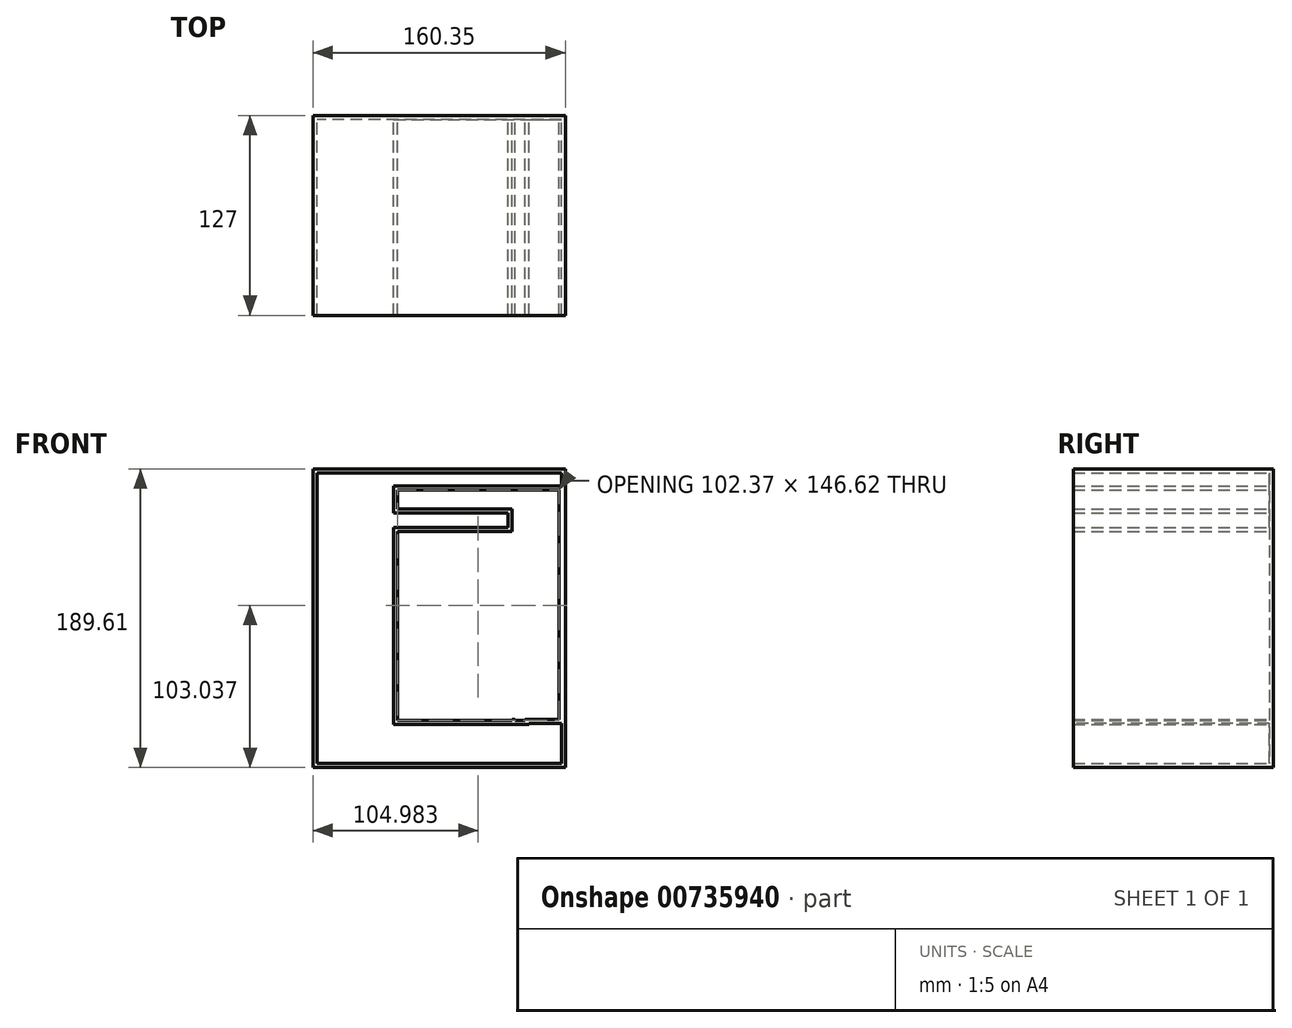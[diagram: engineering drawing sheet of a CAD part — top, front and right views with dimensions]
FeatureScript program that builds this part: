
annotation { "Feature Type Name" : "Feature", "Feature Type Description" : "" }
export const myFeature = defineFeature(function(context is Context, id is Id, definition is map)
    precondition{}
    {
        {
            var Q0;
            Q0=qCreatedBy(makeId("Front.planeOp"),FACE);
            var sketch = newSketch(context, id + "F0", { "sketchPlane" : qUnion([Q0])});
            skLineSegment(sketch, "E0.bottom", {"start": v(-170.01, -40.46) * mm, "end": v(-114.12, -40.46) * mm});
            skLineSegment(sketch, "E0.top", {"start": v(-170.01, -57.23) * mm, "end": v(-114.12, -57.23) * mm});
            skLineSegment(sketch, "E0.left", {"start": v(-170.01, -40.46) * mm, "end": v(-170.01, -57.23) * mm});
            skLineSegment(sketch, "E0.right", {"start": v(-114.12, -40.46) * mm, "end": v(-114.12, -57.23) * mm});
            skLineSegment(sketch, "E1.bottom", {"start": v(-170.01, -40.46) * mm, "end": v(-116.21, -40.46) * mm});
            skLineSegment(sketch, "E1.top", {"start": v(-170.01, 40.36) * mm, "end": v(-116.21, 40.36) * mm});
            skLineSegment(sketch, "E1.left", {"start": v(-170.01, -40.46) * mm, "end": v(-170.01, 40.36) * mm});
            skLineSegment(sketch, "E1.right", {"start": v(-116.21, -40.46) * mm, "end": v(-116.21, 40.36) * mm});
            skLineSegment(sketch, "E2.bottom", {"start": v(-116.21, 40.36) * mm, "end": v(-74.95, 40.36) * mm});
            skLineSegment(sketch, "E2.top", {"start": v(-116.21, -40.46) * mm, "end": v(-74.95, -40.46) * mm});
            skLineSegment(sketch, "E2.left", {"start": v(-116.21, 40.36) * mm, "end": v(-116.21, -40.46) * mm});
            skLineSegment(sketch, "E2.right", {"start": v(-74.95, 40.36) * mm, "end": v(-74.95, -40.46) * mm});
            skLineSegment(sketch, "E3.bottom", {"start": v(-74.95, -40.46) * mm, "end": v(-116.21, -40.46) * mm});
            skLineSegment(sketch, "E3.top", {"start": v(-74.95, -79.7) * mm, "end": v(-116.21, -79.7) * mm});
            skLineSegment(sketch, "E3.left", {"start": v(-74.95, -40.46) * mm, "end": v(-74.95, -79.7) * mm});
            skLineSegment(sketch, "E3.right", {"start": v(-116.21, -40.46) * mm, "end": v(-116.21, -79.7) * mm});
            skLineSegment(sketch, "E4.bottom", {"start": v(-74.95, -79.7) * mm, "end": v(-43.61, -79.7) * mm});
            skLineSegment(sketch, "E4.top", {"start": v(-74.95, -32.7) * mm, "end": v(-43.61, -32.7) * mm});
            skLineSegment(sketch, "E4.left", {"start": v(-74.95, -79.7) * mm, "end": v(-74.95, -32.7) * mm});
            skLineSegment(sketch, "E4.right", {"start": v(-43.61, -79.7) * mm, "end": v(-43.61, -32.7) * mm});
            skLineSegment(sketch, "E5.bottom", {"start": v(-43.61, -32.7) * mm, "end": v(-74.95, -32.7) * mm});
            skLineSegment(sketch, "E5.top", {"start": v(-43.61, 6.98) * mm, "end": v(-74.95, 6.98) * mm});
            skLineSegment(sketch, "E5.left", {"start": v(-43.61, -32.7) * mm, "end": v(-43.61, 6.98) * mm});
            skLineSegment(sketch, "E5.right", {"start": v(-74.95, -32.7) * mm, "end": v(-74.95, 6.98) * mm});
            skLineSegment(sketch, "E6.bottom", {"start": v(-74.95, 40.36) * mm, "end": v(-43.61, 40.36) * mm});
            skLineSegment(sketch, "E6.top", {"start": v(-74.95, 6.98) * mm, "end": v(-43.61, 6.98) * mm});
            skLineSegment(sketch, "E6.left", {"start": v(-74.95, 40.36) * mm, "end": v(-74.95, 6.98) * mm});
            skLineSegment(sketch, "E6.right", {"start": v(-43.61, 40.36) * mm, "end": v(-43.61, 6.98) * mm});
            skLineSegment(sketch, "E7.bottom", {"start": v(-43.61, 40.36) * mm, "end": v(-13.84, 40.36) * mm});
            skLineSegment(sketch, "E7.top", {"start": v(-43.61, 54.76) * mm, "end": v(-13.84, 54.76) * mm});
            skLineSegment(sketch, "E7.left", {"start": v(-43.61, 40.36) * mm, "end": v(-43.61, 54.76) * mm});
            skLineSegment(sketch, "E7.right", {"start": v(-13.84, 40.36) * mm, "end": v(-13.84, 54.76) * mm});
            skLineSegment(sketch, "E8.bottom", {"start": v(-13.84, 54.76) * mm, "end": v(-43.61, 54.76) * mm});
            skLineSegment(sketch, "E8.top", {"start": v(-13.84, 6.98) * mm, "end": v(-43.61, 6.98) * mm});
            skLineSegment(sketch, "E8.left", {"start": v(-13.84, 54.76) * mm, "end": v(-13.84, 6.98) * mm});
            skLineSegment(sketch, "E8.right", {"start": v(-43.61, 54.76) * mm, "end": v(-43.61, 6.98) * mm});
            skLineSegment(sketch, "E9.top", {"start": v(-13.84, -32.7) * mm, "end": v(-43.61, -32.7) * mm});
            skLineSegment(sketch, "E9.left", {"start": v(-13.84, 6.98) * mm, "end": v(-13.84, -32.7) * mm});
            skLineSegment(sketch, "E9.right", {"start": v(-43.61, 6.98) * mm, "end": v(-43.61, -32.7) * mm});
            skLineSegment(sketch, "E10.bottom", {"start": v(-41.52, -32.62) * mm, "end": v(-35.26, -32.62) * mm});
            skLineSegment(sketch, "E10.top", {"start": v(-41.52, -79.7) * mm, "end": v(-35.26, -79.7) * mm});
            skLineSegment(sketch, "E10.left", {"start": v(-41.52, -32.62) * mm, "end": v(-41.52, -79.7) * mm});
            skLineSegment(sketch, "E10.right", {"start": v(-35.26, -32.62) * mm, "end": v(-35.26, -79.7) * mm});
            skLineSegment(sketch, "E11.bottom", {"start": v(-35.26, -78.86) * mm, "end": v(-13.84, -78.86) * mm});
            skLineSegment(sketch, "E11.top", {"start": v(-35.26, -32.7) * mm, "end": v(-13.84, -32.7) * mm});
            skLineSegment(sketch, "E11.left", {"start": v(-35.26, -78.86) * mm, "end": v(-35.26, -32.7) * mm});
            skLineSegment(sketch, "E11.right", {"start": v(-13.84, -78.86) * mm, "end": v(-13.84, -32.7) * mm});
            skLineSegment(sketch, "E12.bottom", {"start": v(-170.01, -57.23) * mm, "end": v(-116.21, -57.23) * mm});
            skLineSegment(sketch, "E12.top", {"start": v(-170.01, -79.7) * mm, "end": v(-116.21, -79.7) * mm});
            skLineSegment(sketch, "E12.left", {"start": v(-170.01, -57.23) * mm, "end": v(-170.01, -79.7) * mm});
            skLineSegment(sketch, "E12.right", {"start": v(-116.21, -57.23) * mm, "end": v(-116.21, -79.7) * mm});
            skLineSegment(sketch, "E13.bottom", {"start": v(-170.01, 40.36) * mm, "end": v(-43.61, 40.36) * mm});
            skLineSegment(sketch, "E13.top", {"start": v(-170.01, 54.76) * mm, "end": v(-43.61, 54.76) * mm});
            skLineSegment(sketch, "E13.left", {"start": v(-170.01, 40.36) * mm, "end": v(-170.01, 54.76) * mm});
            skLineSegment(sketch, "E14.bottom", {"start": v(-170.01, 54.76) * mm, "end": v(-116.21, 54.76) * mm});
            skLineSegment(sketch, "E14.top", {"start": v(-170.01, 66.93) * mm, "end": v(-116.21, 66.93) * mm});
            skLineSegment(sketch, "E14.left", {"start": v(-170.01, 54.76) * mm, "end": v(-170.01, 66.93) * mm});
            skLineSegment(sketch, "E14.right", {"start": v(-116.21, 54.76) * mm, "end": v(-116.21, 66.93) * mm});
            skLineSegment(sketch, "E15.bottom", {"start": v(-116.21, 66.93) * mm, "end": v(-43.61, 66.93) * mm});
            skLineSegment(sketch, "E15.top", {"start": v(-116.21, 54.76) * mm, "end": v(-43.61, 54.76) * mm});
            skLineSegment(sketch, "E15.left", {"start": v(-116.21, 66.93) * mm, "end": v(-116.21, 54.76) * mm});
            skLineSegment(sketch, "E15.right", {"start": v(-43.61, 66.93) * mm, "end": v(-43.61, 54.76) * mm});
            skLineSegment(sketch, "E16.bottom", {"start": v(-43.61, 66.93) * mm, "end": v(-13.84, 66.93) * mm});
            skLineSegment(sketch, "E16.right", {"start": v(-13.84, 66.93) * mm, "end": v(-13.84, 54.76) * mm});
            skLineSegment(sketch, "E17.bottom", {"start": v(-9.66, 66.93) * mm, "end": v(-170.01, 66.93) * mm});
            skLineSegment(sketch, "E17.top", {"start": v(-9.66, 80.2) * mm, "end": v(-170.01, 80.2) * mm});
            skLineSegment(sketch, "E17.left", {"start": v(-9.66, 66.93) * mm, "end": v(-9.66, 80.2) * mm});
            skLineSegment(sketch, "E17.right", {"start": v(-170.01, 66.93) * mm, "end": v(-170.01, 80.2) * mm});
            skLineSegment(sketch, "E18.bottom", {"start": v(-9.66, 66.93) * mm, "end": v(-13.84, 66.93) * mm});
            skLineSegment(sketch, "E18.top", {"start": v(-9.66, -78.86) * mm, "end": v(-13.84, -78.86) * mm});
            skLineSegment(sketch, "E18.left", {"start": v(-9.66, 66.93) * mm, "end": v(-9.66, -78.86) * mm});
            skLineSegment(sketch, "E18.right", {"start": v(-13.84, 66.93) * mm, "end": v(-13.84, -78.86) * mm});
            skLineSegment(sketch, "E19.bottom", {"start": v(-9.66, -78.86) * mm, "end": v(-170.01, -78.86) * mm});
            skLineSegment(sketch, "E19.top", {"start": v(-9.66, -109.42) * mm, "end": v(-170.01, -109.42) * mm});
            skLineSegment(sketch, "E19.left", {"start": v(-9.66, -78.86) * mm, "end": v(-9.66, -109.42) * mm});
            skLineSegment(sketch, "E19.right", {"start": v(-170.01, -78.86) * mm, "end": v(-170.01, -109.42) * mm});
            skSolve(sketch);
        }
        {
            var Q0;
            Q0 = qSketchRegion(id + "F0", true);
            extrude(context, id + "F1", {"entities" : qUnion([Q0]), "depth" : 127 * mm, "offsetDistance" : 25.4 * mm});
        }
        {
            var Q0;
            Q0=makeQuery(id+"F1.opExtrude","CAP_FACE",FACE,{"disambiguationData":[OSD([sQuery(id+"F0.wireOp",EDGE,"E0.left"),sQuery(id+"F0.wireOp",EDGE,"E1.left"),sQuery(id+"F0.wireOp",EDGE,"E2.left"),sQuery(id+"F0.wireOp",EDGE,"E3.top"),sQuery(id+"F0.wireOp",EDGE,"E3.right"),sQuery(id+"F0.wireOp",EDGE,"E4.bottom"),sQuery(id+"F0.wireOp",EDGE,"E4.right"),sQuery(id+"F0.wireOp",EDGE,"E10.top"),sQuery(id+"F0.wireOp",EDGE,"E10.left"),sQuery(id+"F0.wireOp",EDGE,"E10.right"),sQuery(id+"F0.wireOp",EDGE,"E12.left"),sQuery(id+"F0.wireOp",EDGE,"E12.right"),sQuery(id+"F0.wireOp",EDGE,"E13.bottom"),sQuery(id+"F0.wireOp",EDGE,"E13.left"),sQuery(id+"F0.wireOp",EDGE,"E7.left"),sQuery(id+"F0.wireOp",EDGE,"E14.left"),sQuery(id+"F0.wireOp",EDGE,"E15.top"),sQuery(id+"F0.wireOp",EDGE,"E15.left"),sQuery(id+"F0.wireOp",EDGE,"E17.bottom"),sQuery(id+"F0.wireOp",EDGE,"E17.top"),sQuery(id+"F0.wireOp",EDGE,"E17.left"),sQuery(id+"F0.wireOp",EDGE,"E17.right"),sQuery(id+"F0.wireOp",EDGE,"E18.left"),sQuery(id+"F0.wireOp",EDGE,"E18.right"),sQuery(id+"F0.wireOp",EDGE,"E19.bottom"),sQuery(id+"F0.wireOp",EDGE,"E19.top"),sQuery(id+"F0.wireOp",EDGE,"E19.left"),sQuery(id+"F0.wireOp",EDGE,"E19.right")])],"isStart":false});
            shell(context, id + "F2", {"entities" : qUnion([Q0]), "thickness" : 2.54 * mm});
        }
    });
